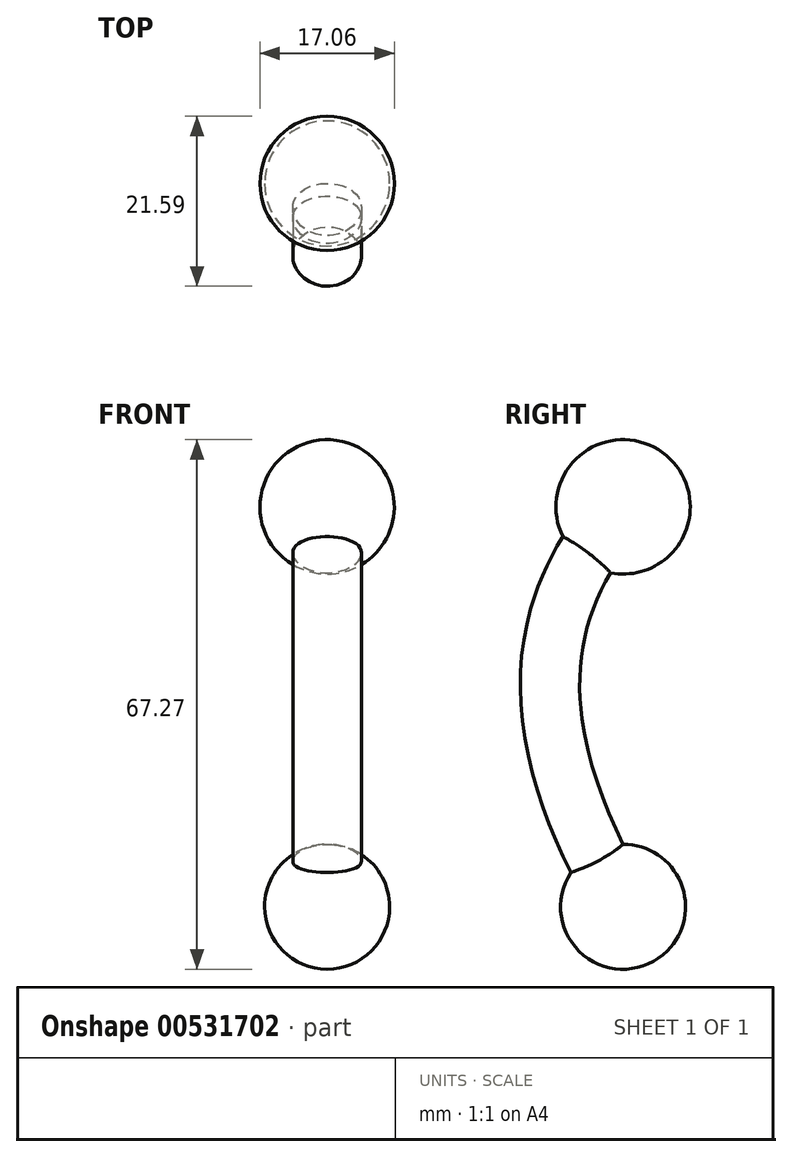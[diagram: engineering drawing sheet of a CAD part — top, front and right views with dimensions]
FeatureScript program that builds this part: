
annotation { "Feature Type Name" : "Feature", "Feature Type Description" : "" }
export const myFeature = defineFeature(function(context is Context, id is Id, definition is map)
    precondition{}
    {
        {
            var Q0;
            Q0=qCreatedBy(makeId("Top.planeOp"),FACE);
            var sketch = newSketch(context, id + "F0", { "sketchPlane" : qUnion([Q0])});
            skArc(sketch, "E0", {"start": v(7.94, 0) * mm, "mid": v(0, 7.94) * mm, "end": v(-7.94, 0) * mm});
            skLineSegment(sketch, "E1", {"start": v(-7.94, 0) * mm, "end": v(7.94, 0) * mm});
            skSolve(sketch);
        }
        {
            var Q0;
            Q0 = qSketchRegion(id + "F0", true);
            var Q1;
            Q1=sQuery(id+"F0.wireOp",EDGE,"E1");
            revolve(context, id + "F1", {"entities" : qUnion([Q0]), "axis" : qUnion([Q1]), "revolveType" : RevolveType.FULL});
        }
        {
            var Q0;
            Q0=qCreatedBy(makeId("Top.planeOp"),FACE);
            var sketch = newSketch(context, id + "F2", { "sketchPlane" : qUnion([Q0])});
            skCircle(sketch, "E2", {"center": v(0, 0) * mm, "radius": 4.37 * mm});
            skSolve(sketch);
        }
        {
            var Q0;
            Q0=qCreatedBy(makeId("Right.planeOp"),FACE);
            var sketch = newSketch(context, id + "F3", { "sketchPlane" : qUnion([Q0])});
            skFitSpline(sketch, "E3", {"points": [v(0, 0) * mm, v(0, 50.8) * mm], "startDerivative": vector(-28.38, 49.22) * mm, "endDerivative": vector(44.47, 49.28) * mm});
            skSolve(sketch);
        }
        {
            var Q0;
            Q0 = qSketchRegion(id + "F2", true);
            var Q1;
            Q1=sQuery(id+"F3.wireOp",EDGE,"E3");
            sweep(context, id + "F4", {"operationType" : NewBodyOperationType.ADD, "profiles" : qUnion([Q0]), "path" : qUnion([Q1])});
        }
        {
            var Q0;
            Q0=makeQuery(id+"F4.opSweep","CAP_FACE",FACE,{"disambiguationData":[OSD([sQuery(id+"F2.wireOp",EDGE,"E2"),sQuery(id+"F3.wireOp",VERTEX,"E3.end")])],"isStart":false});
            var sketch = newSketch(context, id + "F5", { "sketchPlane" : qUnion([Q0])});
            skArc(sketch, "E4", {"start": v(8.52, 47.84) * mm, "mid": v(0.48, 56.84) * mm, "end": v(-8.52, 48.8) * mm});
            skLineSegment(sketch, "E5", {"start": v(-8.52, 48.8) * mm, "end": v(8.52, 47.84) * mm});
            skSolve(sketch);
        }
        {
            var Q0;
            Q0 = qSketchRegion(id + "F5", true);
            var Q1;
            Q1=sQuery(id+"F5.wireOp",EDGE,"E5");
            revolve(context, id + "F6", {"operationType" : NewBodyOperationType.ADD, "entities" : qUnion([Q0]), "axis" : qUnion([Q1]), "revolveType" : RevolveType.FULL});
        }
    });
